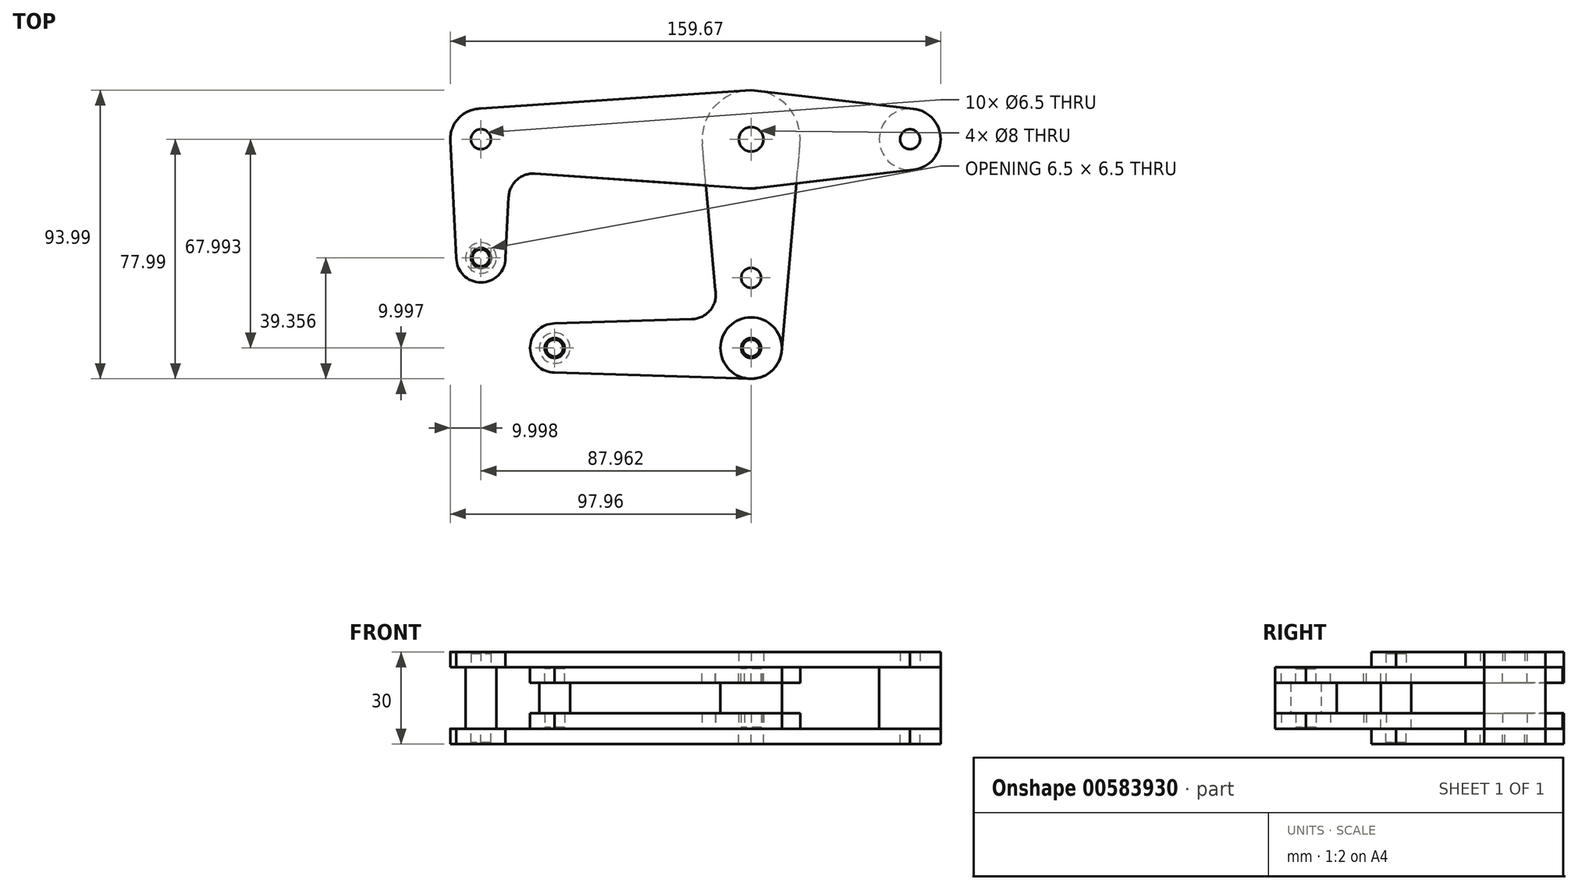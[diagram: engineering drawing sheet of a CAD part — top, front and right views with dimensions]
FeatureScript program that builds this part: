
annotation { "Feature Type Name" : "Feature", "Feature Type Description" : "" }
export const myFeature = defineFeature(function(context is Context, id is Id, definition is map)
    precondition{}
    {
        {
            var Q0;
            Q0=qCreatedBy(makeId("Top.planeOp"),FACE);
            var sketch = newSketch(context, id + "F0", { "sketchPlane" : qUnion([Q0])});
            skCircle(sketch, "E0", {"center": v(0, 0) * mm, "radius": 16 * mm});
            skCircle(sketch, "E1", {"center": v(0, 0) * mm, "radius": 4 * mm});
            skLineSegment(sketch, "E2", {"start": v(-100.52, 0) * mm, "end": v(66.29, 0) * mm, "construction": true});
            skCircle(sketch, "E3", {"center": v(51.71, 0) * mm, "radius": 3.25 * mm});
            skCircle(sketch, "E4", {"center": v(51.71, 0) * mm, "radius": 10 * mm});
            skCircle(sketch, "E5", {"center": v(-87.96, 0) * mm, "radius": 3.25 * mm});
            skCircle(sketch, "E6", {"center": v(-87.96, 0) * mm, "radius": 10 * mm});
            skLineSegment(sketch, "E7", {"start": v(-87.96, 0) * mm, "end": v(-87.96, -38.63) * mm, "construction": true});
            skCircle(sketch, "E8", {"center": v(-87.96, -38.63) * mm, "radius": 3.25 * mm});
            skCircle(sketch, "E9", {"center": v(-87.96, -38.63) * mm, "radius": 8 * mm});
            skLineSegment(sketch, "E10", {"start": v(-95.96, -38.63) * mm, "end": v(-97.98, 0) * mm});
            skLineSegment(sketch, "E11", {"start": v(-79.96, -38.63) * mm, "end": v(-78.93, -18.77) * mm});
            skLineSegment(sketch, "E12", {"start": v(-87.96, 10) * mm, "end": v(0, 16) * mm});
            skLineSegment(sketch, "E13", {"start": v(0, 16) * mm, "end": v(51.71, 10) * mm});
            skLineSegment(sketch, "E14", {"start": v(0, 0) * mm, "end": v(0, -81.93) * mm, "construction": true});
            skCircle(sketch, "E15", {"center": v(0, -68) * mm, "radius": 10 * mm});
            skCircle(sketch, "E16", {"center": v(0, -68) * mm, "radius": 3.25 * mm});
            skLineSegment(sketch, "E17", {"start": v(0, -68) * mm, "end": v(-76.66, -68) * mm, "construction": true});
            skCircle(sketch, "E18", {"center": v(-63.97, -68) * mm, "radius": 8 * mm});
            skCircle(sketch, "E19", {"center": v(-63.97, -68) * mm, "radius": 3.25 * mm});
            skCircle(sketch, "E20", {"center": v(0, -45.11) * mm, "radius": 3.25 * mm});
            skLineSegment(sketch, "E21", {"start": v(-63.97, -76) * mm, "end": v(0, -78) * mm});
            skLineSegment(sketch, "E22", {"start": v(-63.97, -60) * mm, "end": v(-19.25, -58.6) * mm});
            skArc(sketch, "E23.filletArc", {"start": v(-70.4, -11.2) * mm, "mid": v(-76.25, -13.2) * mm, "end": v(-78.93, -18.77) * mm});
            skPoint(sketch, "E24.newPointA", {"position": v(0, -57.99) * mm});
            skArc(sketch, "E24.filletArc", {"start": v(-19.25, -58.6) * mm, "mid": v(-13.27, -55.61) * mm, "end": v(-11.63, -49.13) * mm});
            skLineSegment(sketch, "E25", {"start": v(-11.63, -49.13) * mm, "end": v(-15.94, -1.44) * mm});
            skLineSegment(sketch, "E26", {"start": v(10, -68) * mm, "end": v(15.94, -1.42) * mm});
            skLineSegment(sketch, "E27", {"start": v(51.71, -10) * mm, "end": v(1.88, -15.89) * mm});
            skLineSegment(sketch, "E28", {"start": v(-70.4, -11.2) * mm, "end": v(-1.1, -15.96) * mm});
            skSolve(sketch);
        }
        {
            var Q0;
            Q0=qCreatedBy(makeId("Top.planeOp"),FACE);
            cPlane(context, id + "F1", {"entities" : qUnion([Q0]), "cplaneType" : CPlaneType.OFFSET, "offset" : 10 * mm, "oppositeDirection" : true, "width" : 150 * mm, "height" : 150 * mm});
        }
        {
            var Q0;
            Q0=makeQuery(id+"F0.imprint","IMPRINT",FACE,{"disambiguationData":[TD([[makeQuery(id+"F0.imprint","IMPRINT",EDGE,{"derivedFrom":sQuery(id+"F0.wireOp",EDGE,"E1")}),-1.0]])]});
            var Q1;
            {var subQ0=sQuery(id+"F0.wireOp",EDGE,"E25");var subQ1=sQuery(id+"F0.wireOp",EDGE,"E0");var subQ2=makeQuery(id+"F0.imprint","INTERSECT",VERTEX,{"derivedFrom":[subQ1,subQ0]});Q1=makeQuery(id+"F0.imprint","IMPRINT",FACE,{"disambiguationData":[TD([[makeQuery(id+"F0.imprint","IMPRINT",EDGE,{"disambiguationData":[TD([[subQ2,-1.0]])],"derivedFrom":subQ1}),-1.0]])]});}
            var Q2;
            {var subQ0=sQuery(id+"F0.wireOp",EDGE,"E26");var subQ1=sQuery(id+"F0.wireOp",EDGE,"E0");var subQ2=makeQuery(id+"F0.imprint","INTERSECT",VERTEX,{"derivedFrom":[subQ1,subQ0]});Q2=makeQuery(id+"F0.imprint","IMPRINT",FACE,{"disambiguationData":[TD([[makeQuery(id+"F0.imprint","IMPRINT",EDGE,{"disambiguationData":[TD([[subQ2,1.0]])],"derivedFrom":subQ1}),-1.0]])]});}
            var Q3;
            Q3=makeQuery(id+"F0.imprint","IMPRINT",FACE,{"disambiguationData":[TD([[makeQuery(id+"F0.imprint","IMPRINT",EDGE,{"derivedFrom":sQuery(id+"F0.wireOp",EDGE,"E20")}),-1.0]])]});
            var Q4;
            Q4=makeQuery(id+"F0.imprint","IMPRINT",FACE,{"disambiguationData":[TD([[makeQuery(id+"F0.imprint","IMPRINT",EDGE,{"derivedFrom":sQuery(id+"F0.wireOp",EDGE,"E16")}),-1.0]])]});
            var Q5;
            Q5=makeQuery(id+"F0.imprint","IMPRINT",FACE,{"disambiguationData":[TD([[makeQuery(id+"F0.imprint","IMPRINT",EDGE,{"derivedFrom":sQuery(id+"F0.wireOp",EDGE,"E19")}),-1.0]])]});
            extrude(context, id + "F2", {"entities" : qUnion([Q0, Q1, Q2, Q3, Q4, Q5]), "oppositeDirection" : true, "depth" : 5 * mm, "offsetDistance" : 25 * mm});
        }
        {
            var Q0;
            {var subQ0=sQuery(id+"F0.wireOp",EDGE,"E25");var subQ1=sQuery(id+"F0.wireOp",EDGE,"E0");var subQ2=makeQuery(id+"F0.imprint","INTERSECT",VERTEX,{"derivedFrom":[subQ1,subQ0]});Q0=makeQuery(id+"F0.imprint","IMPRINT",FACE,{"disambiguationData":[TD([[makeQuery(id+"F0.imprint","IMPRINT",EDGE,{"disambiguationData":[TD([[subQ2,-1.0]])],"derivedFrom":subQ1}),-1.0]])]});}
            var Q1;
            {var subQ0=sQuery(id+"F0.wireOp",EDGE,"E26");var subQ1=sQuery(id+"F0.wireOp",EDGE,"E0");var subQ2=makeQuery(id+"F0.imprint","INTERSECT",VERTEX,{"derivedFrom":[subQ1,subQ0]});Q1=makeQuery(id+"F0.imprint","IMPRINT",FACE,{"disambiguationData":[TD([[makeQuery(id+"F0.imprint","IMPRINT",EDGE,{"disambiguationData":[TD([[subQ2,1.0]])],"derivedFrom":subQ1}),-1.0]])]});}
            var Q2;
            Q2=makeQuery(id+"F0.imprint","IMPRINT",FACE,{"disambiguationData":[TD([[makeQuery(id+"F0.imprint","IMPRINT",EDGE,{"derivedFrom":sQuery(id+"F0.wireOp",EDGE,"E1")}),-1.0]])]});
            var Q3;
            {var subQ0=sQuery(id+"F0.wireOp",EDGE,"E26");var subQ1=sQuery(id+"F0.wireOp",EDGE,"E0");var subQ2=makeQuery(id+"F0.imprint","INTERSECT",VERTEX,{"derivedFrom":[subQ1,subQ0]});Q3=makeQuery(id+"F0.imprint","IMPRINT",FACE,{"disambiguationData":[TD([[makeQuery(id+"F0.imprint","IMPRINT",EDGE,{"disambiguationData":[TD([[subQ2,-1.0]])],"derivedFrom":subQ1}),-1.0]])]});}
            var Q4;
            Q4=makeQuery(id+"F0.imprint","IMPRINT",FACE,{"disambiguationData":[TD([[makeQuery(id+"F0.imprint","IMPRINT",EDGE,{"derivedFrom":sQuery(id+"F0.wireOp",EDGE,"E3")}),-1.0]])]});
            var Q5;
            {var subQ3=sQuery(id+"F0.wireOp",EDGE,"E11");Q5=makeQuery(id+"F0.imprint","IMPRINT",FACE,{"disambiguationData":[TD([[makeQuery(id+"F0.imprint","IMPRINT",EDGE,{"derivedFrom":subQ3}),1.0]])]});}
            var Q6;
            Q6=makeQuery(id+"F0.imprint","IMPRINT",FACE,{"disambiguationData":[TD([[makeQuery(id+"F0.imprint","IMPRINT",EDGE,{"derivedFrom":sQuery(id+"F0.wireOp",EDGE,"E5")}),-1.0]])]});
            var Q7;
            Q7=makeQuery(id+"F0.imprint","IMPRINT",FACE,{"disambiguationData":[TD([[makeQuery(id+"F0.imprint","IMPRINT",EDGE,{"derivedFrom":sQuery(id+"F0.wireOp",EDGE,"E8")}),-1.0]])]});
            extrude(context, id + "F3", {"entities" : qUnion([Q0, Q1, Q2, Q3, Q4, Q5, Q6, Q7]), "depth" : 5 * mm, "offsetDistance" : 25 * mm});
        }
        {
            var Q0;
            Q0=makeQuery(id+"F3.opExtrude","CAP_FACE",FACE,{"disambiguationData":[OSD([sQuery(id+"F0.wireOp",EDGE,"E0"),sQuery(id+"F0.wireOp",EDGE,"E1"),sQuery(id+"F0.wireOp",EDGE,"E3"),sQuery(id+"F0.wireOp",EDGE,"E4"),sQuery(id+"F0.wireOp",EDGE,"E5"),sQuery(id+"F0.wireOp",EDGE,"E6"),sQuery(id+"F0.wireOp",EDGE,"E8"),sQuery(id+"F0.wireOp",EDGE,"E9"),sQuery(id+"F0.wireOp",EDGE,"E10"),sQuery(id+"F0.wireOp",EDGE,"E11"),sQuery(id+"F0.wireOp",EDGE,"E12"),sQuery(id+"F0.wireOp",EDGE,"E13"),sQuery(id+"F0.wireOp",EDGE,"E23.filletArc"),sQuery(id+"F0.wireOp",EDGE,"E27"),sQuery(id+"F0.wireOp",EDGE,"E28")])],"isStart":false});
            var sketch = newSketch(context, id + "F4", { "sketchPlane" : qUnion([Q0])});
            skCircle(sketch, "E29", {"center": v(51.71, 0) * mm, "radius": 10 * mm});
            skCircle(sketch, "E30", {"center": v(-87.96, -38.63) * mm, "radius": 5 * mm});
            skSolve(sketch);
        }
        {
            var Q0;
            Q0=makeQuery(id+"F2.opExtrude","CAP_FACE",FACE,{"disambiguationData":[OSD([sQuery(id+"F0.wireOp",EDGE,"E0"),sQuery(id+"F0.wireOp",EDGE,"E1"),sQuery(id+"F0.wireOp",EDGE,"E12"),sQuery(id+"F0.wireOp",EDGE,"E13"),sQuery(id+"F0.wireOp",EDGE,"E15"),sQuery(id+"F0.wireOp",EDGE,"E16"),sQuery(id+"F0.wireOp",EDGE,"E18"),sQuery(id+"F0.wireOp",EDGE,"E19"),sQuery(id+"F0.wireOp",EDGE,"E20"),sQuery(id+"F0.wireOp",EDGE,"E21"),sQuery(id+"F0.wireOp",EDGE,"E22"),sQuery(id+"F0.wireOp",EDGE,"E24.filletArc"),sQuery(id+"F0.wireOp",EDGE,"E25"),sQuery(id+"F0.wireOp",EDGE,"E26")])],"isStart":true});
            var sketch = newSketch(context, id + "F5", { "sketchPlane" : qUnion([Q0])});
            skCircle(sketch, "E31", {"center": v(0, -68) * mm, "radius": 10 * mm});
            skCircle(sketch, "E32", {"center": v(-63.97, -68) * mm, "radius": 5 * mm});
            skSolve(sketch);
        }
        {
            var Q0;
            Q0 = qSketchRegion(id + "F4", true);
            var Q1;
            Q1 = qSketchRegion(id + "F5", true);
            var Q2;
            Q2=qCreatedBy(id+"F1.planeOp",FACE);
            extrude(context, id + "F6", {"entities" : qUnion([Q0, Q1]), "endBound" : BoundingType.UP_TO_SURFACE, "oppositeDirection" : true, "depth" : 25 * mm, "endBoundEntityFace" : qUnion([Q2]), "offsetDistance" : 25 * mm});
        }
        {
            var Q0;
            Q0=makeQuery(id+"F3.opExtrude","SWEPT_BODY",BODY,{"disambiguationData":[OSD([sQuery(id+"F0.wireOp",EDGE,"E0"),sQuery(id+"F0.wireOp",EDGE,"E1"),sQuery(id+"F0.wireOp",EDGE,"E3"),sQuery(id+"F0.wireOp",EDGE,"E4"),sQuery(id+"F0.wireOp",EDGE,"E5"),sQuery(id+"F0.wireOp",EDGE,"E6"),sQuery(id+"F0.wireOp",EDGE,"E8"),sQuery(id+"F0.wireOp",EDGE,"E9"),sQuery(id+"F0.wireOp",EDGE,"E10"),sQuery(id+"F0.wireOp",EDGE,"E11"),sQuery(id+"F0.wireOp",EDGE,"E12"),sQuery(id+"F0.wireOp",EDGE,"E13"),sQuery(id+"F0.wireOp",EDGE,"E23.filletArc"),sQuery(id+"F0.wireOp",EDGE,"E27"),sQuery(id+"F0.wireOp",EDGE,"E28")])]});
            var Q1;
            Q1=makeQuery(id+"F2.opExtrude","SWEPT_BODY",BODY,{"disambiguationData":[OSD([sQuery(id+"F0.wireOp",EDGE,"E0"),sQuery(id+"F0.wireOp",EDGE,"E1"),sQuery(id+"F0.wireOp",EDGE,"E12"),sQuery(id+"F0.wireOp",EDGE,"E13"),sQuery(id+"F0.wireOp",EDGE,"E15"),sQuery(id+"F0.wireOp",EDGE,"E16"),sQuery(id+"F0.wireOp",EDGE,"E18"),sQuery(id+"F0.wireOp",EDGE,"E19"),sQuery(id+"F0.wireOp",EDGE,"E20"),sQuery(id+"F0.wireOp",EDGE,"E21"),sQuery(id+"F0.wireOp",EDGE,"E22"),sQuery(id+"F0.wireOp",EDGE,"E24.filletArc"),sQuery(id+"F0.wireOp",EDGE,"E25"),sQuery(id+"F0.wireOp",EDGE,"E26")])]});
            var Q2;
            Q2=makeQuery(id+"F6.opExtrude","SWEPT_BODY",BODY,{"disambiguationData":[OSD([sQuery(id+"F4.wireOp",EDGE,"E30")])]});
            var Q3;
            Q3=makeQuery(id+"F6.opExtrude","SWEPT_BODY",BODY,{"disambiguationData":[OSD([sQuery(id+"F5.wireOp",EDGE,"E32")])]});
            var Q4;
            Q4=makeQuery(id+"F6.opExtrude","SWEPT_BODY",BODY,{"disambiguationData":[OSD([sQuery(id+"F5.wireOp",EDGE,"E31")])]});
            var Q5;
            Q5=makeQuery(id+"F6.opExtrude","SWEPT_BODY",BODY,{"disambiguationData":[OSD([sQuery(id+"F4.wireOp",EDGE,"E29")])]});
            booleanBodies(context, id + "F7", {"operationType" : BooleanOperationType.SUBTRACTION, "tools" : qUnion([Q0, Q1]), "targets" : qUnion([Q2, Q3, Q4, Q5]), "keepTools" : true});
        }
        {
            var Q0;
            Q0=makeQuery(id+"F6.opExtrude","CAP_FACE",FACE,{"disambiguationData":[OSD([sQuery(id+"F4.wireOp",EDGE,"E30")])],"isStart":true});
            var Q1;
            Q1=makeQuery(id+"F6.opExtrude","CAP_FACE",FACE,{"disambiguationData":[OSD([sQuery(id+"F5.wireOp",EDGE,"E32")])],"isStart":true});
            var Q2;
            Q2=makeQuery(id+"F6.opExtrude","CAP_FACE",FACE,{"disambiguationData":[OSD([sQuery(id+"F5.wireOp",EDGE,"E31")])],"isStart":true});
            var Q3;
            Q3=makeQuery(id+"F7.opBoolean","COPY",EDGE,{"derivedFrom":makeQuery(id+"F3.opExtrude","CAP_EDGE",EDGE,{"disambiguationData":[OSD([sQuery(id+"F0.wireOp",EDGE,"E3")])],"isStart":false})});
            chamfer(context, id + "F8", {"entities" : qUnion([Q0, Q1, Q2, Q3]), "width" : 0.5 * mm, "tangentPropagation" : true});
        }
        {
            var Q0;
            Q0=makeQuery(id+"F6.opExtrude","SWEPT_BODY",BODY,{"disambiguationData":[OSD([sQuery(id+"F5.wireOp",EDGE,"E31")])]});
            var Q1;
            Q1=makeQuery(id+"F6.opExtrude","SWEPT_BODY",BODY,{"disambiguationData":[OSD([sQuery(id+"F4.wireOp",EDGE,"E30")])]});
            var Q2;
            Q2=makeQuery(id+"F6.opExtrude","SWEPT_BODY",BODY,{"disambiguationData":[OSD([sQuery(id+"F5.wireOp",EDGE,"E32")])]});
            var Q3;
            Q3=makeQuery(id+"F6.opExtrude","SWEPT_BODY",BODY,{"disambiguationData":[OSD([sQuery(id+"F4.wireOp",EDGE,"E29")])]});
            var Q4;
            Q4=qCreatedBy(id+"F1.planeOp",FACE);
            mirror(context, id + "F9", {"operationType" : NewBodyOperationType.ADD, "entities" : qUnion([Q0, Q1, Q2, Q3]), "mirrorPlane" : qUnion([Q4])});
        }
        {
            var Q0;
            Q0=makeQuery(id+"F2.opExtrude","SWEPT_BODY",BODY,{"disambiguationData":[OSD([sQuery(id+"F0.wireOp",EDGE,"E0"),sQuery(id+"F0.wireOp",EDGE,"E1"),sQuery(id+"F0.wireOp",EDGE,"E12"),sQuery(id+"F0.wireOp",EDGE,"E13"),sQuery(id+"F0.wireOp",EDGE,"E15"),sQuery(id+"F0.wireOp",EDGE,"E16"),sQuery(id+"F0.wireOp",EDGE,"E18"),sQuery(id+"F0.wireOp",EDGE,"E19"),sQuery(id+"F0.wireOp",EDGE,"E20"),sQuery(id+"F0.wireOp",EDGE,"E21"),sQuery(id+"F0.wireOp",EDGE,"E22"),sQuery(id+"F0.wireOp",EDGE,"E24.filletArc"),sQuery(id+"F0.wireOp",EDGE,"E25"),sQuery(id+"F0.wireOp",EDGE,"E26")])]});
            var Q1;
            Q1=makeQuery(id+"F3.opExtrude","SWEPT_BODY",BODY,{"disambiguationData":[OSD([sQuery(id+"F0.wireOp",EDGE,"E0"),sQuery(id+"F0.wireOp",EDGE,"E1"),sQuery(id+"F0.wireOp",EDGE,"E3"),sQuery(id+"F0.wireOp",EDGE,"E4"),sQuery(id+"F0.wireOp",EDGE,"E5"),sQuery(id+"F0.wireOp",EDGE,"E6"),sQuery(id+"F0.wireOp",EDGE,"E8"),sQuery(id+"F0.wireOp",EDGE,"E9"),sQuery(id+"F0.wireOp",EDGE,"E10"),sQuery(id+"F0.wireOp",EDGE,"E11"),sQuery(id+"F0.wireOp",EDGE,"E12"),sQuery(id+"F0.wireOp",EDGE,"E13"),sQuery(id+"F0.wireOp",EDGE,"E23.filletArc"),sQuery(id+"F0.wireOp",EDGE,"E27"),sQuery(id+"F0.wireOp",EDGE,"E28")])]});
            var Q2;
            Q2=qCreatedBy(id+"F1.planeOp",FACE);
            mirror(context, id + "F10", {"entities" : qUnion([Q0, Q1]), "mirrorPlane" : qUnion([Q2])});
        }
    });
